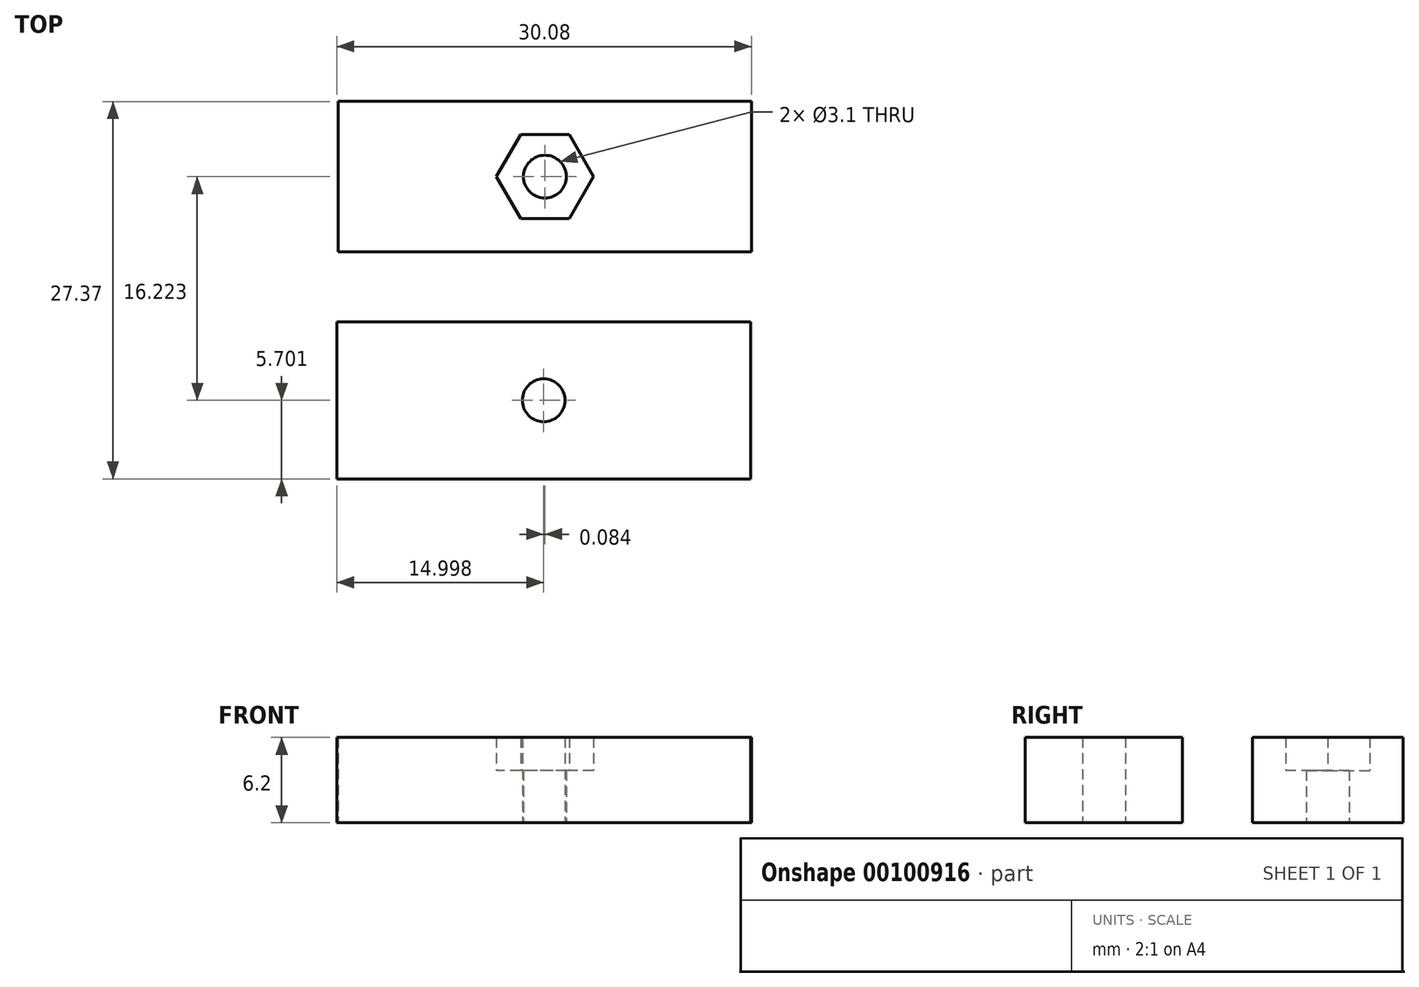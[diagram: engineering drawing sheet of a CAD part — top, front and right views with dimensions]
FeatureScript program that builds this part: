
annotation { "Feature Type Name" : "Feature", "Feature Type Description" : "" }
export const myFeature = defineFeature(function(context is Context, id is Id, definition is map)
    precondition{}
    {
        {
            var Q0;
            Q0=qCreatedBy(makeId("Top.planeOp"),FACE);
            var sketch = newSketch(context, id + "F0", { "sketchPlane" : qUnion([Q0])});
            skLineSegment(sketch, "E0.bottom", {"start": v(-16.18, 3.25) * mm, "end": v(13.82, 3.25) * mm});
            skLineSegment(sketch, "E0.top", {"start": v(-16.18, -7.65) * mm, "end": v(13.82, -7.65) * mm});
            skLineSegment(sketch, "E0.left", {"start": v(-16.18, 3.25) * mm, "end": v(-16.18, -7.65) * mm});
            skLineSegment(sketch, "E0.right", {"start": v(13.82, 3.25) * mm, "end": v(13.82, -7.65) * mm});
            skLineSegment(sketch, "E1", {"start": v(-16.18, -2.2) * mm, "end": v(13.82, -2.2) * mm, "construction": true});
            skPoint(sketch, "E2.start.orphan", {"position": v(-1.18, 3.25) * mm});
            skPoint(sketch, "E3.trimOffspring.end.orphan", {"position": v(-1.18, -7.65) * mm});
            skLineSegment(sketch, "E4.bottom", {"start": v(-16.26, -12.72) * mm, "end": v(13.74, -12.72) * mm});
            skLineSegment(sketch, "E4.top", {"start": v(-16.26, -24.12) * mm, "end": v(13.74, -24.12) * mm});
            skLineSegment(sketch, "E4.left", {"start": v(-16.26, -12.72) * mm, "end": v(-16.26, -24.12) * mm});
            skLineSegment(sketch, "E4.right", {"start": v(13.74, -12.72) * mm, "end": v(13.74, -24.12) * mm});
            skLineSegment(sketch, "E5", {"start": v(-16.26, -18.42) * mm, "end": v(13.74, -18.42) * mm, "construction": true});
            skLineSegment(sketch, "E6.bottom", {"start": v(-30.6, 1.86) * mm, "end": v(-19.57, 1.86) * mm, "construction": true});
            skLineSegment(sketch, "E6.top", {"start": v(-30.6, -8.16) * mm, "end": v(-19.57, -8.16) * mm, "construction": true});
            skLineSegment(sketch, "E6.left", {"start": v(-30.6, 1.86) * mm, "end": v(-30.6, -8.16) * mm, "construction": true});
            skLineSegment(sketch, "E6.right", {"start": v(-19.57, 1.86) * mm, "end": v(-19.57, -8.16) * mm, "construction": true});
            skLineSegment(sketch, "E7", {"start": v(-30.6, -3.15) * mm, "end": v(-19.57, -3.15) * mm, "construction": true});
            skCircle(sketch, "E8", {"center": v(-25.09, -3.15) * mm, "radius": 1.55 * mm, "construction": true});
            skCircle(sketch, "E9", {"center": v(-25.09, -3.15) * mm, "radius": 2.85 * mm, "construction": true});
            skLineSegment(sketch, "E10.0", {"start": v(-23.44, -6) * mm, "end": v(-26.73, -6) * mm});
            skLineSegment(sketch, "E10.1", {"start": v(-26.73, -6) * mm, "end": v(-28.38, -3.15) * mm});
            skLineSegment(sketch, "E10.2", {"start": v(-28.38, -3.15) * mm, "end": v(-26.73, -0.3) * mm});
            skLineSegment(sketch, "E10.3", {"start": v(-26.73, -0.3) * mm, "end": v(-23.44, -0.3) * mm});
            skLineSegment(sketch, "E10.4", {"start": v(-23.44, -0.3) * mm, "end": v(-21.8, -3.15) * mm});
            skLineSegment(sketch, "E10.5", {"start": v(-21.8, -3.15) * mm, "end": v(-23.44, -6) * mm});
            skPoint(sketch, "E10.0.midPoint", {"position": v(-25.09, -6) * mm});
            skLineSegment(sketch, "E11.bottom", {"start": v(-30.75, -10.5) * mm, "end": v(-19.53, -10.5) * mm, "construction": true});
            skLineSegment(sketch, "E11.top", {"start": v(-30.75, -21.36) * mm, "end": v(-19.53, -21.36) * mm, "construction": true});
            skLineSegment(sketch, "E11.left", {"start": v(-30.75, -10.5) * mm, "end": v(-30.75, -21.36) * mm, "construction": true});
            skLineSegment(sketch, "E11.right", {"start": v(-19.53, -10.5) * mm, "end": v(-19.53, -21.36) * mm, "construction": true});
            skLineSegment(sketch, "E12", {"start": v(-30.75, -15.93) * mm, "end": v(-19.53, -15.93) * mm, "construction": true});
            skCircle(sketch, "E13", {"center": v(-25.14, -15.93) * mm, "radius": 1.55 * mm, "construction": true});
            skCircle(sketch, "E14", {"center": v(-25.14, -15.93) * mm, "radius": 2.8 * mm, "construction": true});
            skLineSegment(sketch, "E15", {"start": v(-1.26, -24.12) * mm, "end": v(-1.26, -21.12) * mm, "construction": true});
            skLineSegment(sketch, "E16", {"start": v(-1.26, -12.72) * mm, "end": v(-1.26, -15.72) * mm, "construction": true});
            skLineSegment(sketch, "E17", {"start": v(-1.18, 3.25) * mm, "end": v(-1.18, 0.25) * mm, "construction": true});
            skLineSegment(sketch, "E18", {"start": v(-1.18, -7.65) * mm, "end": v(-1.18, -5.25) * mm, "construction": true});
            skCircle(sketch, "E19", {"center": v(-1.18, -2.2) * mm, "radius": 1.55 * mm});
            skCircle(sketch, "E20", {"center": v(-1.18, -2.2) * mm, "radius": 2.85 * mm, "construction": true});
            skCircle(sketch, "E21.cCircle", {"center": v(-1.18, -2.2) * mm, "radius": 3.05 * mm, "construction": true});
            skLineSegment(sketch, "E21.0", {"start": v(0.58, -5.25) * mm, "end": v(-2.94, -5.25) * mm});
            skLineSegment(sketch, "E21.1", {"start": v(-2.94, -5.25) * mm, "end": v(-4.7, -2.2) * mm});
            skLineSegment(sketch, "E21.2", {"start": v(-4.7, -2.2) * mm, "end": v(-2.94, 0.85) * mm});
            skLineSegment(sketch, "E21.3", {"start": v(-2.94, 0.85) * mm, "end": v(0.58, 0.85) * mm});
            skLineSegment(sketch, "E21.4", {"start": v(0.58, 0.85) * mm, "end": v(2.34, -2.2) * mm});
            skLineSegment(sketch, "E21.5", {"start": v(2.34, -2.2) * mm, "end": v(0.58, -5.25) * mm});
            skPoint(sketch, "E21.0.midPoint", {"position": v(-1.18, -5.25) * mm});
            skCircle(sketch, "E22", {"center": v(-1.26, -18.42) * mm, "radius": 1.55 * mm});
            skSolve(sketch);
        }
        {
            var Q0;
            Q0=makeQuery(id+"F0.imprint","IMPRINT",FACE,{"disambiguationData":[TD([[makeQuery(id+"F0.imprint","IMPRINT",EDGE,{"derivedFrom":sQuery(id+"F0.wireOp",EDGE,"E0.bottom")}),-1.0]])]});
            var Q1;
            Q1=makeQuery(id+"F0.imprint","IMPRINT",FACE,{"disambiguationData":[TD([[makeQuery(id+"F0.imprint","IMPRINT",EDGE,{"derivedFrom":sQuery(id+"F0.wireOp",EDGE,"E4.bottom")}),-1.0]])]});
            extrude(context, id + "F1", {"entities" : qUnion([Q0, Q1]), "depth" : 6.2 * mm});
        }
        {
            var Q0;
            Q0=makeQuery(id+"F0.imprint","IMPRINT",FACE,{"disambiguationData":[TD([[makeQuery(id+"F0.imprint","IMPRINT",EDGE,{"derivedFrom":sQuery(id+"F0.wireOp",EDGE,"E19")}),-1.0]])]});
            extrude(context, id + "F2", {"entities" : qUnion([Q0]), "operationType" : NewBodyOperationType.ADD, "depth" : 3.8 * mm});
        }
        {
            var Q0;
            Q0=makeQuery(id+"F1.opExtrude","CAP_FACE",FACE,{"disambiguationData":[OSD([sQuery(id+"F0.wireOp",EDGE,"E0.bottom"),sQuery(id+"F0.wireOp",EDGE,"E0.top"),sQuery(id+"F0.wireOp",EDGE,"E0.left"),sQuery(id+"F0.wireOp",EDGE,"E0.right"),sQuery(id+"F0.wireOp",EDGE,"E21.0"),sQuery(id+"F0.wireOp",EDGE,"E21.1"),sQuery(id+"F0.wireOp",EDGE,"E21.2"),sQuery(id+"F0.wireOp",EDGE,"E21.3"),sQuery(id+"F0.wireOp",EDGE,"E21.4"),sQuery(id+"F0.wireOp",EDGE,"E21.5")])],"isStart":false});
            var sketch = newSketch(context, id + "F3", { "sketchPlane" : qUnion([Q0])});
            skLineSegment(sketch, "E23.0.0", {"start": v(13.82, 3.25) * mm, "end": v(-16.18, 3.25) * mm});
            skLineSegment(sketch, "E23.0.1", {"start": v(-16.18, 3.25) * mm, "end": v(-16.18, -7.65) * mm});
            skLineSegment(sketch, "E23.0.2", {"start": v(-16.18, -7.65) * mm, "end": v(13.82, -7.65) * mm});
            skLineSegment(sketch, "E23.0.3", {"start": v(13.82, -7.65) * mm, "end": v(13.82, 3.25) * mm});
            skLineSegment(sketch, "E24", {"start": v(-1.18, 3.25) * mm, "end": v(-1.18, 0.85) * mm, "construction": true});
            skPoint(sketch, "E25", {"position": v(-1.18, 2.05) * mm});
            skSolve(sketch);
        }
    });
